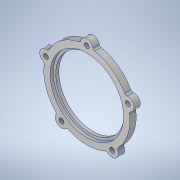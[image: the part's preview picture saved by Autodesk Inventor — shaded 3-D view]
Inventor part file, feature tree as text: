
AUTODESK INVENTOR PART (.ipt)
format: ipt  version: 2020 (Build 240168000, 168)  size: 217,600 bytes
history: native  units: mm
features: extrude x3, sketch x3, projected_geometry x2, other x1, fillet x1, chamfer x1
ambient origin geometry x8: Origin, YZ Plane, XZ Plane, XY Plane, X Axis, Y Axis, Z Axis, Center Point
bodies: Body1 (feature_tree)
feature tree (11):
  other  "솔리드1"
  extrude  "돌출1"  Depth=44.0mm
  extrude  "돌출2"  Depth=47.05mm
  extrude  "돌출3"  Depth=55.2mm
  fillet  "모깎기1"  Radius=2.5mm
  chamfer  "모따기1"  Distance=8.0mm
  sketch  "스케치1"
  sketch  "스케치2"
  projected_geometry  "투영된 루프1"
  sketch  "스케치3"
  projected_geometry  "투영된 루프2"
